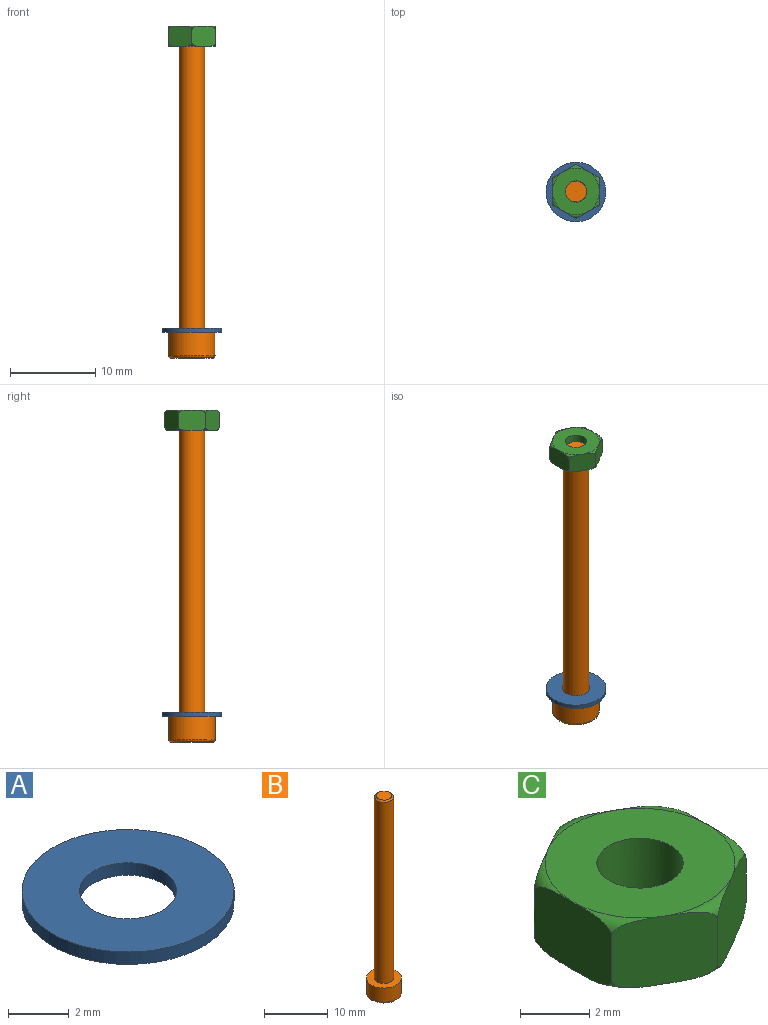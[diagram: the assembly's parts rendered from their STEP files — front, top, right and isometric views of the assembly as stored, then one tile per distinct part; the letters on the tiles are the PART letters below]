
ASSEMBLY  parts=3 mates=3
PART A: 4 faces, bbox 7x7x0.5 mm
  f0: cylinder r=1.6mm len=3.2mm, axis (0,0,-1), area 5mm2, adj f2,f3
  f1: cylinder r=3.5mm len=7mm, axis (0,0,-1), area 11mm2, adj f2,f3
  f2: plane 7x7mm, normal (0,0,1), area 30.4mm2, adj f0,f1
  f3: plane 7x7mm, normal (0,0,-1), area 30.4mm2, adj f0,f1
PART B: 14 faces, bbox 6x6x38 mm
  f0: plane 4.95x4.95mm, normal (0,0,-1), area 13.5mm2, adj f3,f4,f5,f6,f7,f8,f9
  f1: cylinder r=2.75mm len=5.5mm, axis (0,0,1), area 47.1mm2, adj f2,f3
  f2: plane 5.5x5.5mm, normal (0,0,1), area 16.7mm2, adj f1,f11
  f3: torus R=2.48mm, axis (0,0,-1), area 7.2mm2, adj f0,f1
  f4: plane 1.5x1.49mm, normal (-1,0,0), area 2.2mm2, adj f0,f5,f9,f10
  f5: plane 1.5x1.29mm, normal (-0.5,-0.87,0), area 2.2mm2, adj f0,f4,f6,f10
  f6: plane 1.5x1.29mm, normal (0.5,-0.87,0), area 2.2mm2, adj f0,f5,f7,f10
  f7: plane 1.5x1.49mm, normal (1,0,0), area 2.2mm2, adj f0,f6,f8,f10
  f8: plane 1.5x1.29mm, normal (0.5,0.87,0), area 2.2mm2, adj f0,f7,f9,f10
  f9: plane 1.5x1.29mm, normal (-0.5,0.87,0), area 2.2mm2, adj f0,f4,f8,f10
  f10: plane 2.98x2.58mm, normal (0,0,-1), area 5.8mm2, adj f4,f5,f6,f7,f8,f9
  f11: cylinder r=1.5mm len=34.73mm, axis (0,0,-1), area 327.3mm2, adj f2,f13
  f12: plane 2.46x2.46mm, normal (0,0,1), area 4.7mm2, adj f13
  f13: cone r=1.23mm half-angle=45deg, axis (0,0,-1), area 3.3mm2, adj f11,f12
PART C: 11 faces, bbox 6.9x6.9x2.4 mm
  f0: plane 5.49x5.49mm, normal (0,0,1), area 18.8mm2, adj f1,f10
  f1: torus R=2.75mm, axis (0,0,-1), area 2.8mm2, adj f0,f2,f3,f4,f5,f6,f7
  f2: plane 2.75x2.4mm, normal (0.5,0.87,0), area 7.3mm2, adj f1,f3,f7,f9
  f3: plane 3.18x2.4mm, normal (1,0,0), area 7.3mm2, adj f1,f2,f4,f9
  f4: plane 2.75x2.4mm, normal (0.5,-0.87,0), area 7.3mm2, adj f1,f3,f5,f9
  f5: plane 2.75x2.4mm, normal (-0.5,-0.87,0), area 7.3mm2, adj f1,f4,f6,f9
  f6: plane 3.18x2.4mm, normal (-1,0,0), area 7.3mm2, adj f1,f5,f7,f9
  f7: plane 2.75x2.4mm, normal (-0.5,0.87,0), area 7.3mm2, adj f1,f2,f6,f9
  f8: plane 5.49x5.49mm, normal (0,0,-1), area 18.8mm2, adj f9,f10
  f9: torus R=2.75mm, axis (0,0,-1), area 2.8mm2, adj f2,f3,f4,f5,f6,f7,f8
  f10: cylinder r=1.25mm len=2.5mm, axis (0,0,-1), area 18.8mm2, adj f0,f8
PLACE A t=(131.43,22.22,-15.48)mm
PLACE B t=(31.43,12.22,-15.48)mm
PLACE C t=(101.43,32.22,18.05)mm
MATE planar A.f0 <-> B.f1  axis (0,0,-1) through (121.43,12.22,-15.48)mm
MATE cylindrical C.f1 <-> B.f1  axis (0,0,-1) through (121.43,12.22,19.25)mm
MATE cylindrical A.f0 <-> B.f1  axis (0,0,-1) through (121.43,12.22,-15.23)mm
